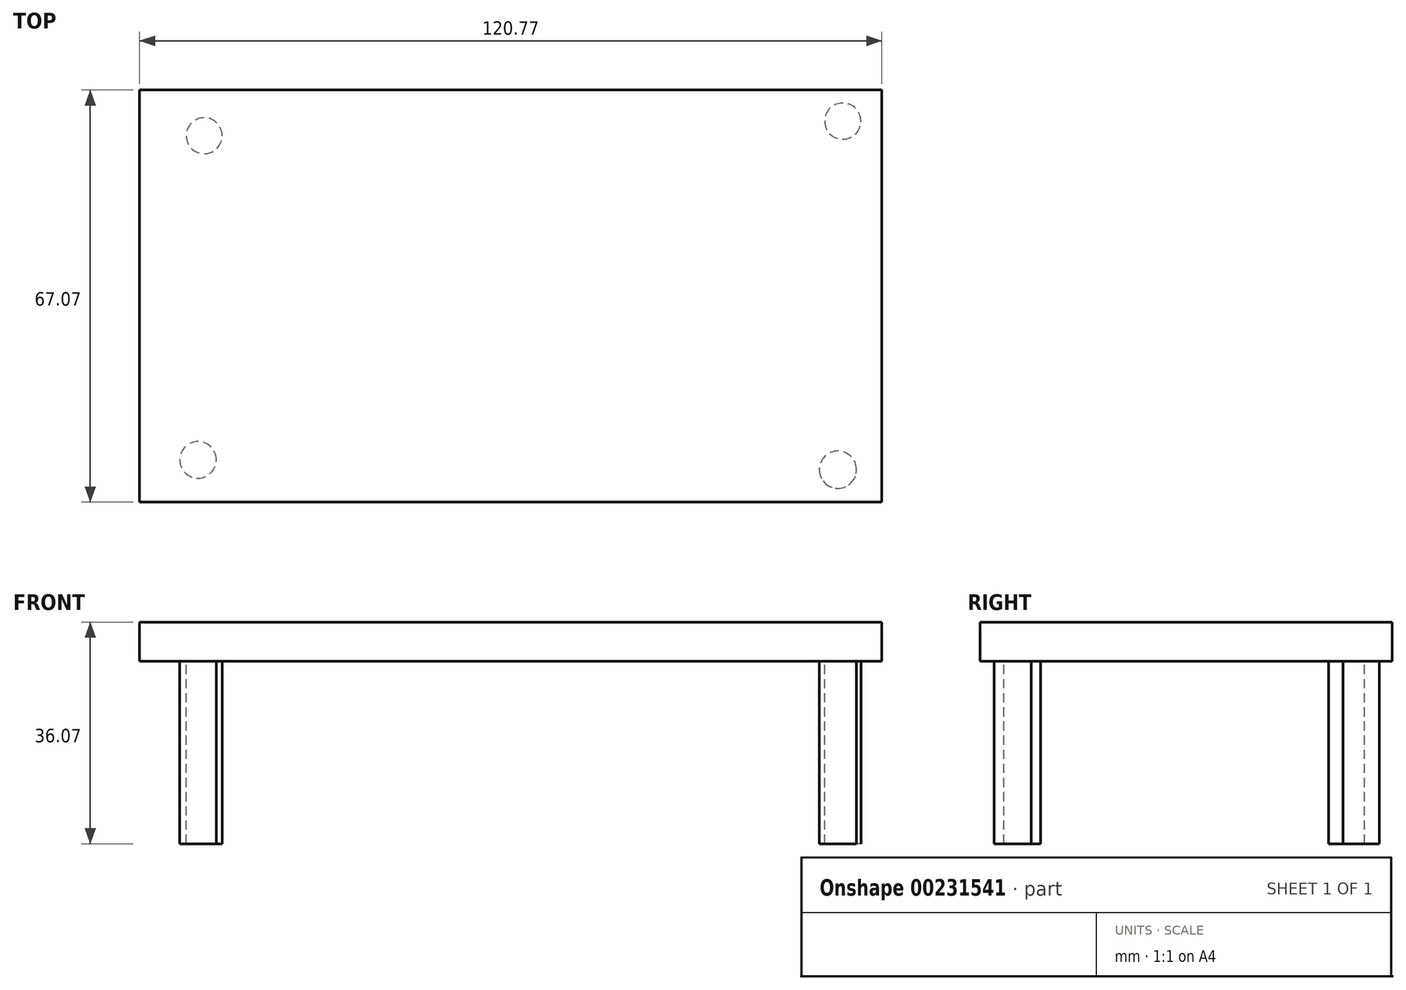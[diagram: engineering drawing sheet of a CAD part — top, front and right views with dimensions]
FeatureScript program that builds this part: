
annotation { "Feature Type Name" : "Feature", "Feature Type Description" : "" }
export const myFeature = defineFeature(function(context is Context, id is Id, definition is map)
    precondition{}
    {
        {
            var Q0;
            Q0=qCreatedBy(makeId("Top.planeOp"),FACE);
            var sketch = newSketch(context, id + "F0", { "sketchPlane" : qUnion([Q0])});
            skLineSegment(sketch, "E0.bottom", {"start": v(-24.06, 21.82) * mm, "end": v(96.7, 21.82) * mm});
            skLineSegment(sketch, "E0.top", {"start": v(-24.06, -45.25) * mm, "end": v(96.7, -45.25) * mm});
            skLineSegment(sketch, "E0.left", {"start": v(-24.06, 21.82) * mm, "end": v(-24.06, -45.25) * mm});
            skLineSegment(sketch, "E0.right", {"start": v(96.7, 21.82) * mm, "end": v(96.7, -45.25) * mm});
            skPoint(sketch, "E0.middle", {"position": v(36.32, -11.71) * mm});
            skSolve(sketch);
        }
        {
            var Q0;
            Q0 = qSketchRegion(id + "F0", true);
            extrude(context, id + "F1", {"entities" : qUnion([Q0]), "depth" : 6.35 * mm});
        }
        {
            var Q0;
            Q0=makeQuery(id+"F1.opExtrude","CAP_FACE",FACE,{"disambiguationData":[OSD([sQuery(id+"F0.wireOp",EDGE,"E0.bottom"),sQuery(id+"F0.wireOp",EDGE,"E0.top"),sQuery(id+"F0.wireOp",EDGE,"E0.left"),sQuery(id+"F0.wireOp",EDGE,"E0.right")])],"isStart":true});
            var sketch = newSketch(context, id + "F2", { "sketchPlane" : qUnion([Q0])});
            skCircle(sketch, "E1", {"center": v(-14.53, 38.37) * mm, "radius": 2.98 * mm});
            skCircle(sketch, "E2", {"center": v(-13.54, -14.38) * mm, "radius": 2.93 * mm});
            skCircle(sketch, "E3", {"center": v(89.57, 39.96) * mm, "radius": 3.03 * mm});
            skCircle(sketch, "E4", {"center": v(90.36, -16.76) * mm, "radius": 2.95 * mm});
            skSolve(sketch);
        }
        {
            var Q0;
            Q0 = qSketchRegion(id + "F2", true);
            extrude(context, id + "F3", {"entities" : qUnion([Q0]), "operationType" : NewBodyOperationType.ADD, "depth" : 29.72 * mm});
        }
    });
